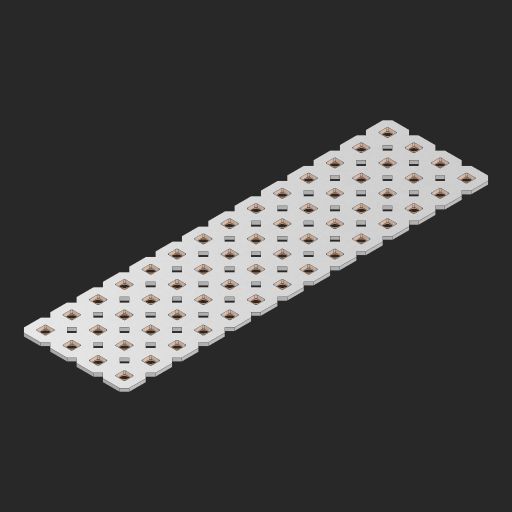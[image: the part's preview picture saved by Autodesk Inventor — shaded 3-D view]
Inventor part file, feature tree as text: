
AUTODESK INVENTOR PART (.ipt)
format: ipt  version: 2023 (Build 270158000, 158)  size: 933,888 bytes
history: native  units: in
note: dims shown in document units (in); Inventor stores cm internally (conversion verified against a paired STEP export)
features: other x57, extrude x55, sketch x2, pattern_linear x1
ambient origin geometry x8: Origin, YZ Plane, XZ Plane, XY Plane, X Axis, Y Axis, Z Axis, Center Point
bodies: Solid1 (feature_tree), Body (feature_tree)
feature tree (115):
  pattern_linear  "Rectangular Pattern1"  Spacing1=0.09in  [1 undecoded]
  sketch  "Sketch1"  dims[d1=0.5in]
  sketch  "Sketch2"  dims[d2=0.182in d3=0.09in d4=0.09in d5=0.09in d6=0.09in d7=0.09in d8=0.09in d9=0.09in d10=0.09in d11=0.02in d13=0.0in d14=0.172in d15=0.0625in d16=0.0in d19=0.5in d22=0.5in]
  other  "Srf1"
  other  "Srf126"
  other  "Srf127"
  other  "Srf128"
  other  "Srf129"
  other  "Srf130"
  other  "Srf131"
  other  "Srf250"
  other  "Srf251"
  other  "Srf252"
  other  "Srf253"
  other  "Srf254"
  other  "Srf255"
  other  "Srf256"
  other  "Srf268"
  other  "Srf269"
  other  "Srf270"
  other  "Srf271"
  other  "Srf272"
  other  "Srf273"
  other  "Srf274"
  other  "Srf275"
  other  "Srf276"
  other  "Srf277"
  other  "Srf278"
  other  "Srf279"
  other  "Srf280"
  other  "Srf281"
  other  "Srf293"
  other  "Srf294"
  other  "Srf295"
  other  "Srf296"
  other  "Srf297"
  other  "Srf298"
  other  "Srf299"
  other  "Srf300"
  other  "Srf301"
  other  "Srf302"
  other  "Srf303"
  other  "Srf304"
  other  "Srf305"
  other  "Srf306"
  other  "Srf318"
  other  "Srf319"
  other  "Srf320"
  other  "Srf321"
  other  "Srf322"
  other  "Srf323"
  other  "Srf324"
  other  "Srf325"
  other  "Srf326"
  other  "Srf327"
  other  "Srf328"
  other  "Srf329"
  other  "Srf330"
  other  "Srf331"
  other  "Circle"
  extrude  "ExtrusionSrf126"  Depth=0.09in
  extrude  "ExtrusionSrf127"  Depth=0.09in
  extrude  "ExtrusionSrf128"  Depth=0.09in
  extrude  "ExtrusionSrf129"  Depth=0.09in
  extrude  "ExtrusionSrf130"  Depth=0.09in
  extrude  "ExtrusionSrf131"  Depth=0.09in
  extrude  "ExtrusionSrf250"  Depth=0.09in
  extrude  "ExtrusionSrf251"  Depth=0.02in
  extrude  "ExtrusionSrf252"  TaperAngle=0.0deg  [1 undecoded]
  extrude  "ExtrusionSrf253"  Depth=0.5in
  extrude  "ExtrusionSrf254"  Depth=0.0625in TaperAngle=0.0deg
  extrude  "ExtrusionSrf255"  Depth=0.5in
  extrude  "ExtrusionSrf256"  Depth=0.5in
  extrude  "ExtrusionSrf268"  [1 undecoded]
  extrude  "ExtrusionSrf269"  [1 undecoded]
  extrude  "ExtrusionSrf270"  [1 undecoded]
  extrude  "ExtrusionSrf271"  [1 undecoded]
  extrude  "ExtrusionSrf272"  [1 undecoded]
  extrude  "ExtrusionSrf273"  [1 undecoded]
  extrude  "ExtrusionSrf274"  [1 undecoded]
  extrude  "ExtrusionSrf275"  [1 undecoded]
  extrude  "ExtrusionSrf276"  [1 undecoded]
  extrude  "ExtrusionSrf277"  [1 undecoded]
  extrude  "ExtrusionSrf278"  [1 undecoded]
  extrude  "ExtrusionSrf279"  [1 undecoded]
  extrude  "ExtrusionSrf280"  [1 undecoded]
  extrude  "ExtrusionSrf281"  [1 undecoded]
  extrude  "ExtrusionSrf293"  [1 undecoded]
  extrude  "ExtrusionSrf294"  [1 undecoded]
  extrude  "ExtrusionSrf295"  [1 undecoded]
  extrude  "ExtrusionSrf296"  [1 undecoded]
  extrude  "ExtrusionSrf297"  [1 undecoded]
  extrude  "ExtrusionSrf298"  [1 undecoded]
  extrude  "ExtrusionSrf299"  [1 undecoded]
  extrude  "ExtrusionSrf300"  [1 undecoded]
  extrude  "ExtrusionSrf301"  [1 undecoded]
  extrude  "ExtrusionSrf302"  [1 undecoded]
  extrude  "ExtrusionSrf303"  [1 undecoded]
  extrude  "ExtrusionSrf304"  [1 undecoded]
  extrude  "ExtrusionSrf305"  [1 undecoded]
  extrude  "ExtrusionSrf306"  [1 undecoded]
  extrude  "ExtrusionSrf318"  [1 undecoded]
  extrude  "ExtrusionSrf319"  [1 undecoded]
  extrude  "ExtrusionSrf320"  [1 undecoded]
  extrude  "ExtrusionSrf321"  [1 undecoded]
  extrude  "ExtrusionSrf322"  [1 undecoded]
  extrude  "ExtrusionSrf323"  [1 undecoded]
  extrude  "ExtrusionSrf324"  [1 undecoded]
  extrude  "ExtrusionSrf325"  [1 undecoded]
  extrude  "ExtrusionSrf326"  [1 undecoded]
  extrude  "ExtrusionSrf327"  [1 undecoded]
  extrude  "ExtrusionSrf328"  [1 undecoded]
  extrude  "ExtrusionSrf329"  [1 undecoded]
  extrude  "ExtrusionSrf330"  [1 undecoded]
  extrude  "ExtrusionSrf331"  [1 undecoded]
note: 44 required parameter values undecoded (feature->parameter linkage not recoverable at this tier; creation-order binding heuristic only, values carry confidence <= 0.55)
